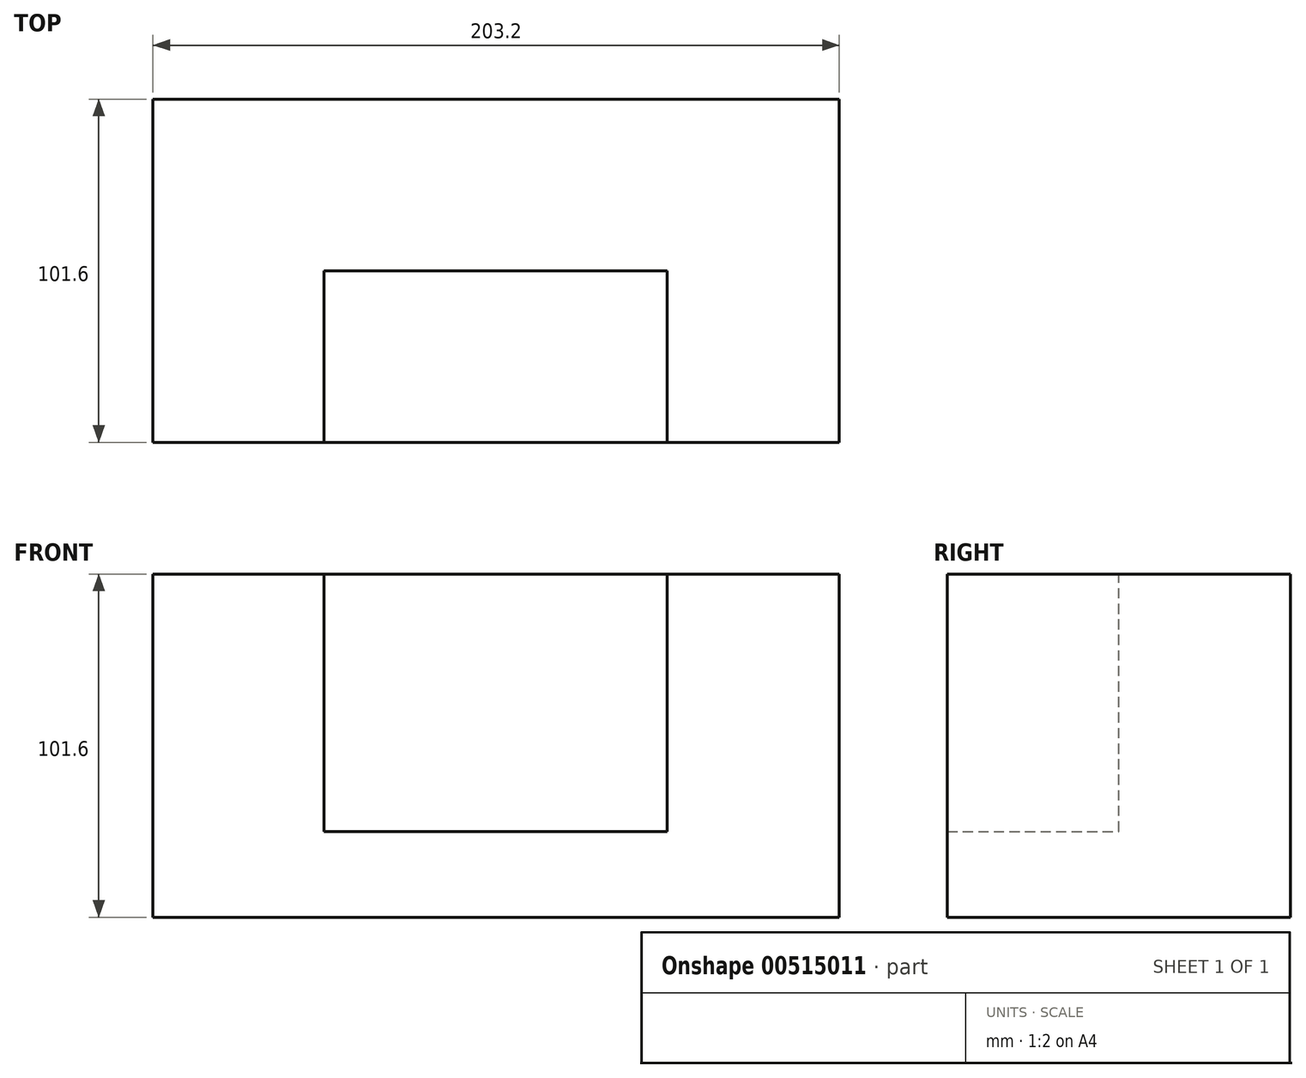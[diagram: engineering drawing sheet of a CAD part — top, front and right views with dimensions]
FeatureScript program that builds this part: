
annotation { "Feature Type Name" : "Feature", "Feature Type Description" : "" }
export const myFeature = defineFeature(function(context is Context, id is Id, definition is map)
    precondition{}
    {
        {
            var Q0;
            Q0=qCreatedBy(makeId("Top.planeOp"),FACE);
            var sketch = newSketch(context, id + "F0", { "sketchPlane" : qUnion([Q0])});
            skLineSegment(sketch, "E0.bottom", {"start": v(-97.18, 50.8) * mm, "end": v(106.02, 50.8) * mm});
            skLineSegment(sketch, "E0.left", {"start": v(-97.18, 50.8) * mm, "end": v(-97.18, 0) * mm});
            skLineSegment(sketch, "E0.right", {"start": v(106.02, 50.8) * mm, "end": v(106.02, 0) * mm});
            skLineSegment(sketch, "E1.top", {"start": v(106.02, -50.8) * mm, "end": v(55.22, -50.8) * mm});
            skLineSegment(sketch, "E1.left", {"start": v(106.02, 0) * mm, "end": v(106.02, -50.8) * mm});
            skLineSegment(sketch, "E1.right", {"start": v(-97.18, 0) * mm, "end": v(-97.18, -50.8) * mm});
            skLineSegment(sketch, "E2", {"start": v(-46.38, -50.8) * mm, "end": v(-97.18, -50.8) * mm});
            skLineSegment(sketch, "E3", {"start": v(55.22, -50.8) * mm, "end": v(-46.38, -50.8) * mm});
            skSolve(sketch);
        }
        {
            var Q0;
            Q0 = qSketchRegion(id + "F0", true);
            extrude(context, id + "F1", {"entities" : qUnion([Q0]), "depth" : 101.6 * mm, "offsetDistance" : 25.4 * mm});
        }
        {
            var Q0;
            Q0=makeQuery(id+"F1.opExtrude","CAP_FACE",FACE,{"disambiguationData":[OSD([sQuery(id+"F0.wireOp",EDGE,"E0.bottom"),sQuery(id+"F0.wireOp",EDGE,"E0.left"),sQuery(id+"F0.wireOp",EDGE,"E0.right"),sQuery(id+"F0.wireOp",EDGE,"E1.top"),sQuery(id+"F0.wireOp",EDGE,"E1.left"),sQuery(id+"F0.wireOp",EDGE,"E1.right"),sQuery(id+"F0.wireOp",EDGE,"E2"),sQuery(id+"F0.wireOp",EDGE,"E3")])],"isStart":false});
            var sketch = newSketch(context, id + "F2", { "sketchPlane" : qUnion([Q0])});
            skLineSegment(sketch, "E4.bottom", {"start": v(-46.55, -50.8) * mm, "end": v(55.05, -50.8) * mm});
            skLineSegment(sketch, "E4.top", {"start": v(-46.55, 0) * mm, "end": v(55.05, 0) * mm});
            skLineSegment(sketch, "E4.left", {"start": v(-46.55, -50.8) * mm, "end": v(-46.55, 0) * mm});
            skLineSegment(sketch, "E4.right", {"start": v(55.05, -50.8) * mm, "end": v(55.05, 0) * mm});
            skSolve(sketch);
        }
        {
            var Q0;
            Q0 = qSketchRegion(id + "F2", true);
            extrude(context, id + "F3", {"entities" : qUnion([Q0]), "operationType" : NewBodyOperationType.REMOVE, "oppositeDirection" : true, "depth" : 76.2 * mm, "offsetDistance" : 25.4 * mm});
        }
    });
